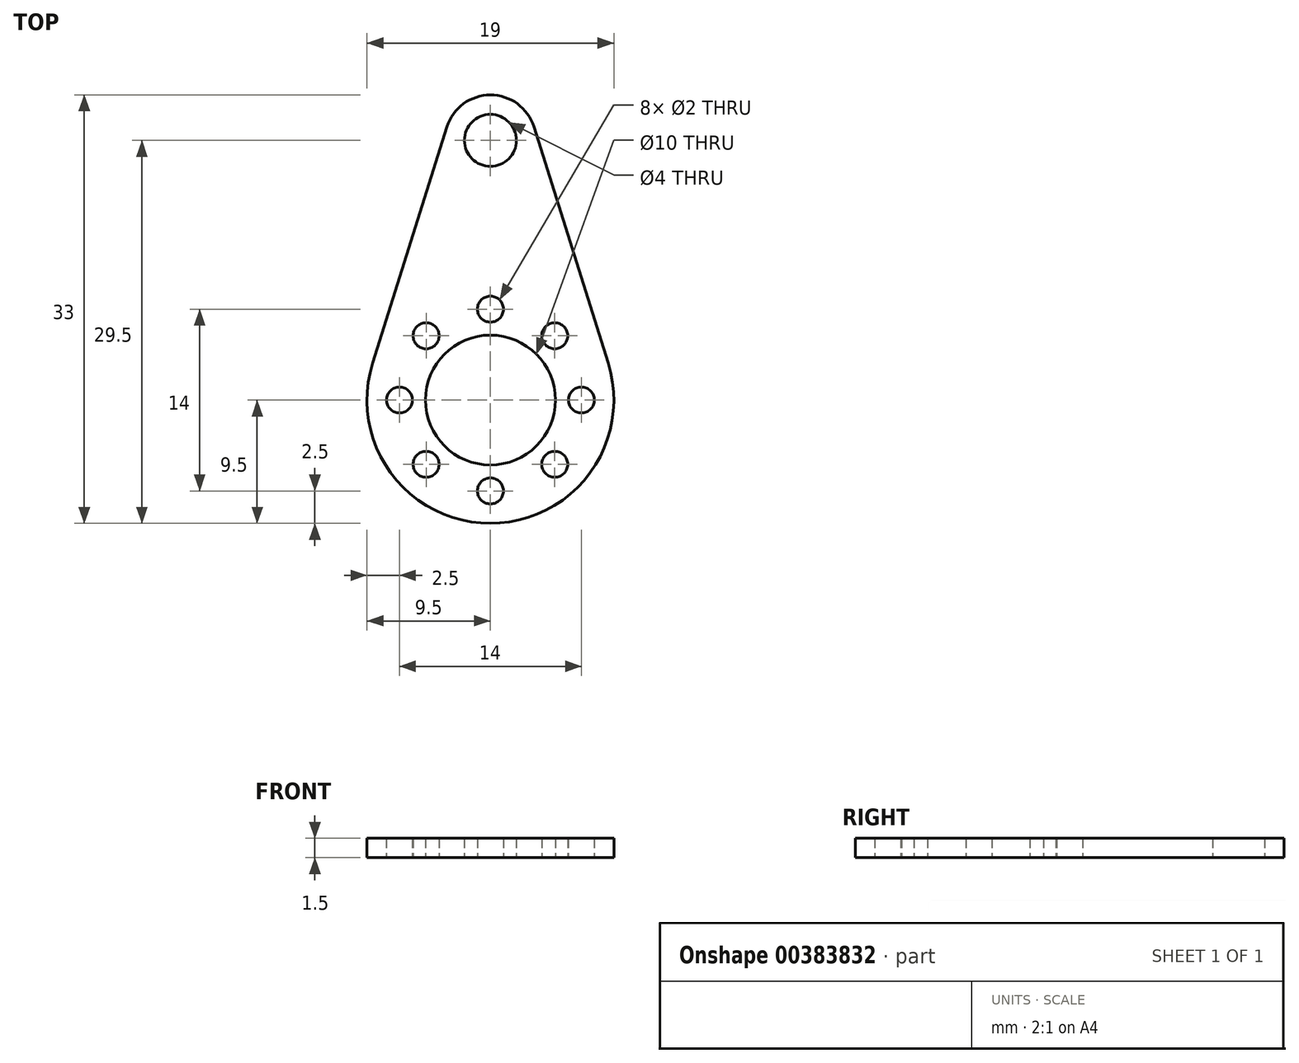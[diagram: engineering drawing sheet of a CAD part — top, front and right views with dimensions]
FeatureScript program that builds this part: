
annotation { "Feature Type Name" : "Feature", "Feature Type Description" : "" }
export const myFeature = defineFeature(function(context is Context, id is Id, definition is map)
    precondition{}
    {
        {
            var Q0;
            Q0=qCreatedBy(makeId("Top.planeOp"),FACE);
            var sketch = newSketch(context, id + "F0", { "sketchPlane" : qUnion([Q0])});
            skCircle(sketch, "E0", {"center": v(0, 0) * mm, "radius": 5 * mm});
            skCircle(sketch, "E1", {"center": v(7, 0) * mm, "radius": 1 * mm});
            skCircle(sketch, "E2", {"center": v(0, 20) * mm, "radius": 2 * mm});
            skArc(sketch, "E3", {"start": v(3.34, 21.05) * mm, "mid": v(0, 23.5) * mm, "end": v(-3.34, 21.05) * mm});
            skCircle(sketch, "E4.1.0", {"center": v(4.95, 4.95) * mm, "radius": 1 * mm});
            skCircle(sketch, "E4.2.0", {"center": v(0, 7) * mm, "radius": 1 * mm});
            skCircle(sketch, "E4.3.0", {"center": v(-4.95, 4.95) * mm, "radius": 1 * mm});
            skCircle(sketch, "E4.4.0", {"center": v(-7, 0) * mm, "radius": 1 * mm});
            skCircle(sketch, "E4.5.0", {"center": v(-4.95, -4.95) * mm, "radius": 1 * mm});
            skCircle(sketch, "E4.6.0", {"center": v(0, -7) * mm, "radius": 1 * mm});
            skCircle(sketch, "E4.7.0", {"center": v(4.95, -4.95) * mm, "radius": 1 * mm});
            skArc(sketch, "E5", {"start": v(-9.06, 2.85) * mm, "mid": v(0, -9.5) * mm, "end": v(9.06, 2.85) * mm});
            skLineSegment(sketch, "E6", {"start": v(-3.34, 21.05) * mm, "end": v(-9.06, 2.85) * mm});
            skLineSegment(sketch, "E7.MirrorCS", {"start": v(3.34, 21.05) * mm, "end": v(9.06, 2.85) * mm});
            skSolve(sketch);
        }
        {
            var Q0;
            Q0 = qSketchRegion(id + "F0", true);
            extrude(context, id + "F1", {"entities" : qUnion([Q0]), "depth" : 1.5 * mm, "offsetDistance" : 25 * mm});
        }
    });
